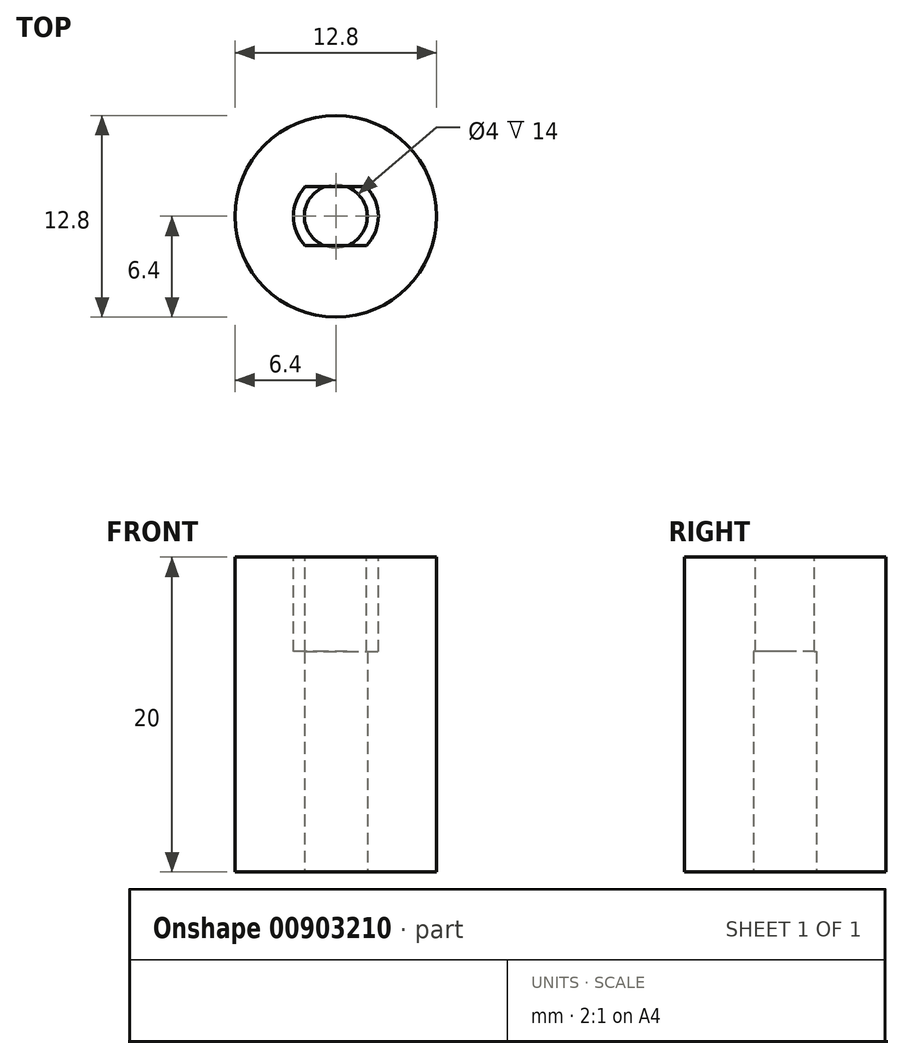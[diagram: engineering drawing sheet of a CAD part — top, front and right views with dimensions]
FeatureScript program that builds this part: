
annotation { "Feature Type Name" : "Feature", "Feature Type Description" : "" }
export const myFeature = defineFeature(function(context is Context, id is Id, definition is map)
    precondition{}
    {
        {
            var Q0;
            Q0=qCreatedBy(makeId("Top.planeOp"),FACE);
            var sketch = newSketch(context, id + "F0", { "sketchPlane" : qUnion([Q0])});
            skCircle(sketch, "E0", {"center": v(0, 0) * mm, "radius": 6.4 * mm});
            skSolve(sketch);
        }
        {
            var Q0;
            Q0=makeQuery(id+"F0.imprint","IMPRINT",FACE,{"disambiguationData":[TD([[makeQuery(id+"F0.imprint","IMPRINT",EDGE,{"derivedFrom":sQuery(id+"F0.wireOp",EDGE,"E0")}),1.0]])]});
            var Q1;
            Q1=makeQuery(id+"F0.imprint","IMPRINT",FACE,{"disambiguationData":[TD([[makeQuery(id+"F0.imprint","IMPRINT",EDGE,{"derivedFrom":sQuery(id+"F0.wireOp",EDGE,"Kd4oP0SL-7RFL-OBj8-Bmld-SwuPkdznoUvC")}),1.0]])]});
            extrude(context, id + "F1", {"entities" : qUnion([Q0, Q1]), "depth" : 20 * mm, "offsetDistance" : 25.4 * mm});
        }
        {
            var Q0;
            Q0=makeQuery(id+"FASwoxiQhmsnyT8_1.boolean.opBoolean","SPLIT",FACE,{"disambiguationData":[TD([makeQuery(id+"FASwoxiQhmsnyT8_1.opExtrude","SWEPT_FACE",FACE,{"disambiguationData":[OSD([sQuery(id+"F29BJCUL0qqsJng_1.wireOp",EDGE,"elMcLGNu-7Bnl-lFHy-3noi-i8HbDGMgueHU")])]})])],"derivedFrom":makeQuery(id+"F1.opExtrude","CAP_FACE",FACE,{"disambiguationData":[OSD([sQuery(id+"F0.wireOp",EDGE,"E0")])],"isStart":false})});
            var sketch = newSketch(context, id + "F2", { "sketchPlane" : qUnion([Q0])});
            skArc(sketch, "E1", {"start": v(-1.94, 1.87) * mm, "mid": v(-2.7, 0) * mm, "end": v(-1.94, -1.87) * mm});
            skLineSegment(sketch, "E2", {"start": v(-1.94, 1.87) * mm, "end": v(1.94, 1.88) * mm});
            skLineSegment(sketch, "E3", {"start": v(-1.94, -1.87) * mm, "end": v(1.94, -1.87) * mm});
            skArc(sketch, "E4.trimOffspring", {"start": v(1.94, -1.87) * mm, "mid": v(2.7, 0) * mm, "end": v(1.94, 1.87) * mm});
            skSolve(sketch);
        }
        {
            var Q0;
            Q0=makeQuery(id+"F2.imprint","IMPRINT",FACE,{"disambiguationData":[TD([[makeQuery(id+"F2.imprint","IMPRINT",EDGE,{"derivedFrom":sQuery(id+"F2.wireOp",EDGE,"E1")}),1.0]])]});
            extrude(context, id + "F3", {"entities" : qUnion([Q0]), "operationType" : NewBodyOperationType.REMOVE, "oppositeDirection" : true, "depth" : 6 * mm, "offsetDistance" : 25.4 * mm});
        }
        {
            var Q0;
            Q0=makeQuery(id+"F1.opExtrude","CAP_FACE",FACE,{"disambiguationData":[OSD([sQuery(id+"F0.wireOp",EDGE,"E0")])],"isStart":true});
            var sketch = newSketch(context, id + "F4", { "sketchPlane" : qUnion([Q0])});
            skCircle(sketch, "E5", {"center": v(0, 0) * mm, "radius": 2 * mm});
            skSolve(sketch);
        }
        {
            var Q0;
            Q0=makeQuery(id+"F4.imprint","IMPRINT",FACE,{"disambiguationData":[TD([[makeQuery(id+"F4.imprint","IMPRINT",EDGE,{"derivedFrom":sQuery(id+"F4.wireOp",EDGE,"E5")}),1.0]])]});
            var Q1;
            Q1=makeQuery(id+"F3.boolean.opBoolean","COPY",FACE,{"derivedFrom":makeQuery(id+"F3.opExtrude","CAP_FACE",FACE,{"disambiguationData":[OSD([sQuery(id+"F2.wireOp",EDGE,"E1"),sQuery(id+"F2.wireOp",EDGE,"E2"),sQuery(id+"F2.wireOp",EDGE,"E3"),sQuery(id+"F2.wireOp",EDGE,"E4.trimOffspring")])],"isStart":false})});
            extrude(context, id + "F5", {"entities" : qUnion([Q0]), "operationType" : NewBodyOperationType.REMOVE, "endBound" : BoundingType.UP_TO_SURFACE, "oppositeDirection" : true, "depth" : 25.4 * mm, "endBoundEntityFace" : qUnion([Q1]), "offsetDistance" : 25.4 * mm});
        }
    });
